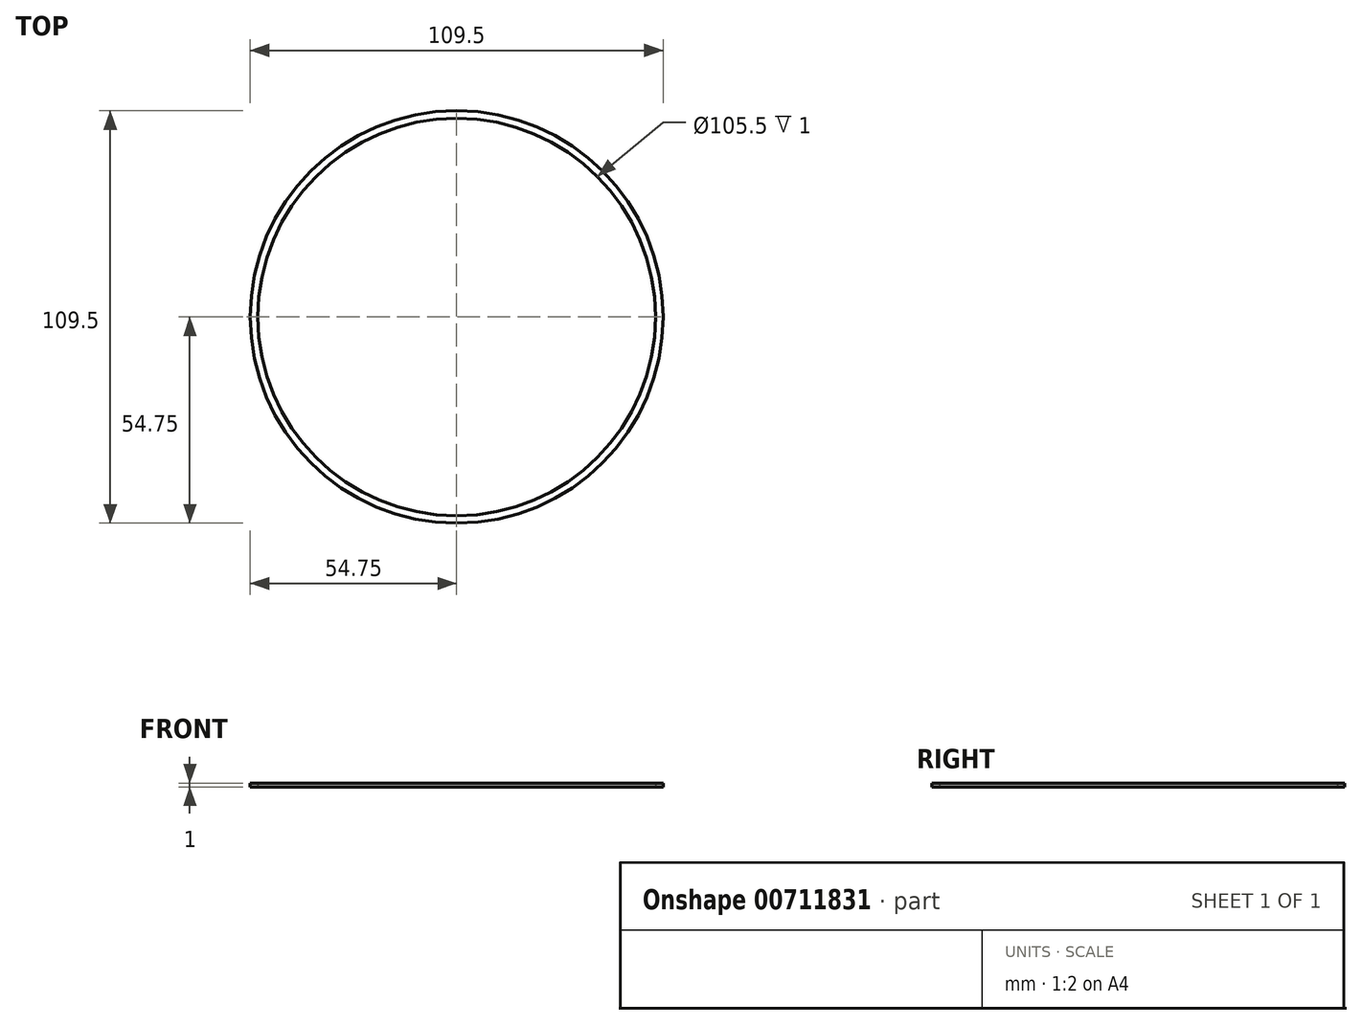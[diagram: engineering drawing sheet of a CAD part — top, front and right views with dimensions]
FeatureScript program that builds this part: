
annotation { "Feature Type Name" : "Feature", "Feature Type Description" : "" }
export const myFeature = defineFeature(function(context is Context, id is Id, definition is map)
    precondition{}
    {
        {
            var Q0;
            Q0=qCreatedBy(makeId("Top.planeOp"),FACE);
            var sketch = newSketch(context, id + "F0", { "sketchPlane" : qUnion([Q0])});
            skCircle(sketch, "E0", {"center": v(0, 0) * mm, "radius": 52.75 * mm});
            skCircle(sketch, "E1", {"center": v(0, 0) * mm, "radius": 54.75 * mm});
            skSolve(sketch);
        }
        {
            var Q0;
            Q0=makeQuery(id+"F0.imprint","IMPRINT",FACE,{"disambiguationData":[TD([[makeQuery(id+"F0.imprint","IMPRINT",EDGE,{"derivedFrom":sQuery(id+"F0.wireOp",EDGE,"E0")}),-1.0]])]});
            extrude(context, id + "F1", {"entities" : qUnion([Q0]), "depth" : 1 * mm, "offsetDistance" : 25 * mm});
        }
    });
